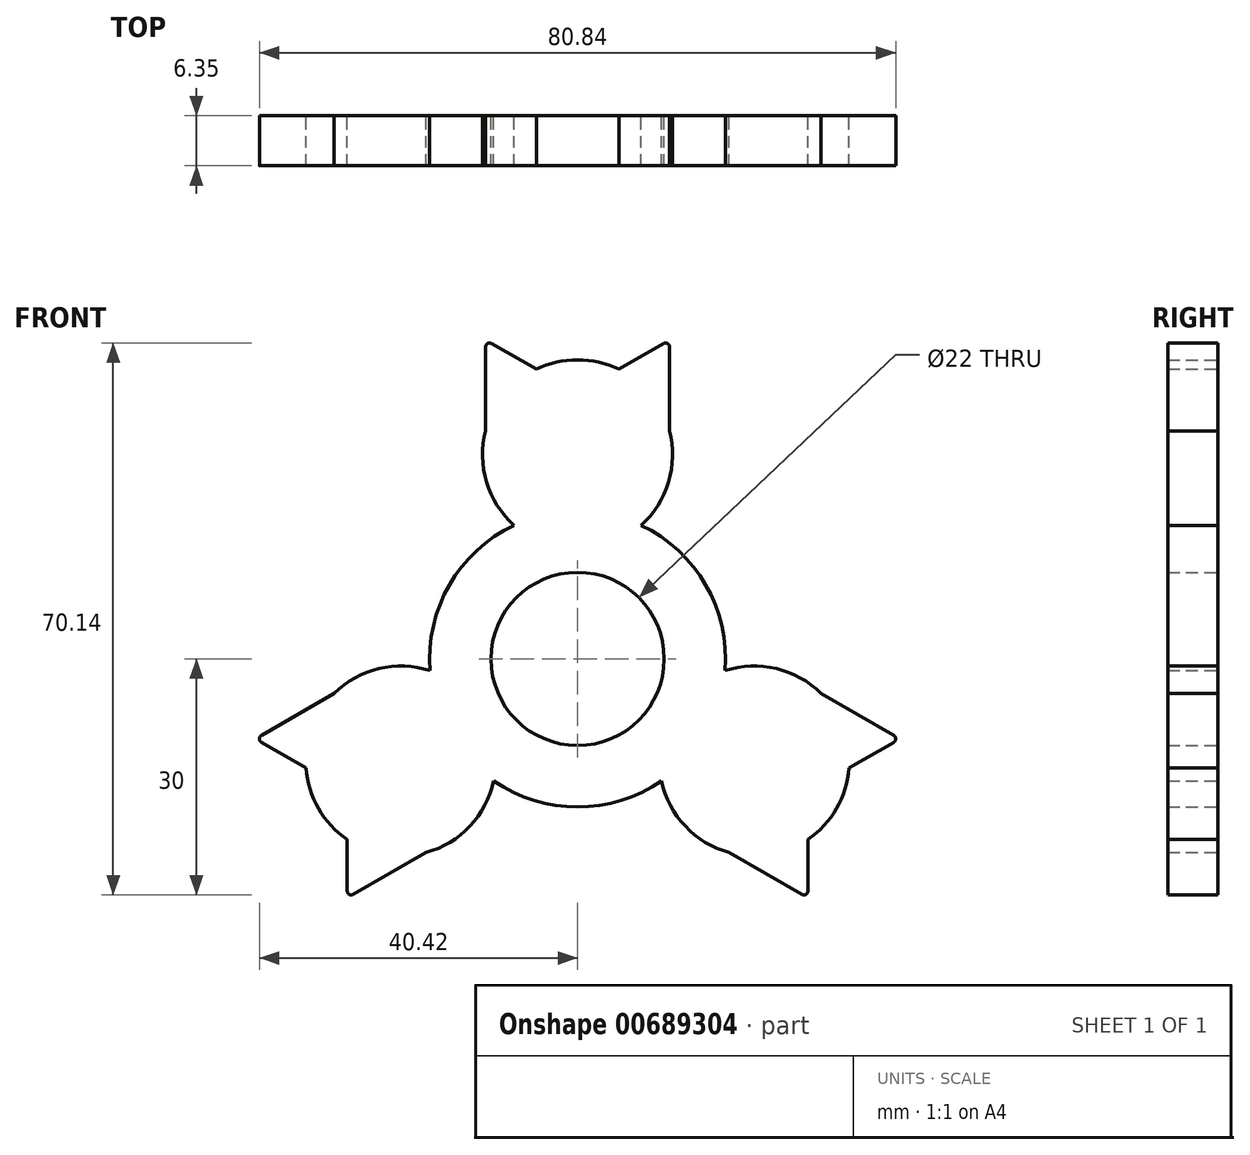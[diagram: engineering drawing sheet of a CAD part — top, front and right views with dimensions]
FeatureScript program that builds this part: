
annotation { "Feature Type Name" : "Feature", "Feature Type Description" : "" }
export const myFeature = defineFeature(function(context is Context, id is Id, definition is map)
    precondition{}
    {
        {
            var Q0;
            Q0=qCreatedBy(makeId("Front.planeOp"),FACE);
            var sketch = newSketch(context, id + "F0", { "sketchPlane" : qUnion([Q0])});
            skCircle(sketch, "E0", {"center": v(0, 0) * mm, "radius": 44.45 * mm, "construction": true});
            skCircle(sketch, "E1", {"center": v(0, 0) * mm, "radius": 11 * mm});
            skCircle(sketch, "E2", {"center": v(0, 0) * mm, "radius": 4 * mm});
            skArc(sketch, "E3", {"start": v(18.74, -1.5) * mm, "mid": v(16.28, 9.4) * mm, "end": v(8.08, 16.97) * mm});
            skArc(sketch, "E4", {"start": v(8.08, 16.97) * mm, "mid": v(0, 38) * mm, "end": v(-8.08, 16.97) * mm});
            skLineSegment(sketch, "E5", {"start": v(-11.67, 28.98) * mm, "end": v(-11.67, 40.52) * mm});
            skLineSegment(sketch, "E6", {"start": v(-11.67, 40.52) * mm, "end": v(-5.24, 36.8) * mm});
            skLineSegment(sketch, "E7.MirrorCS", {"start": v(11.67, 40.52) * mm, "end": v(5.24, 36.8) * mm});
            skLineSegment(sketch, "E8.MirrorCS", {"start": v(11.67, 28.98) * mm, "end": v(11.67, 40.52) * mm});
            skArc(sketch, "E9.1.0", {"start": v(-18.74, -1.5) * mm, "mid": v(-32.9, -19) * mm, "end": v(-10.66, -15.48) * mm});
            skLineSegment(sketch, "E9.1.1", {"start": v(-40.92, -10.15) * mm, "end": v(-34.5, -13.86) * mm});
            skLineSegment(sketch, "E9.1.2", {"start": v(-30.94, -4.38) * mm, "end": v(-40.92, -10.15) * mm});
            skLineSegment(sketch, "E9.1.3", {"start": v(-29.25, -30.37) * mm, "end": v(-29.25, -22.94) * mm});
            skLineSegment(sketch, "E9.1.4", {"start": v(-19.26, -24.6) * mm, "end": v(-29.25, -30.37) * mm});
            skArc(sketch, "E9.2.0", {"start": v(10.66, -15.48) * mm, "mid": v(32.9, -19) * mm, "end": v(18.74, -1.5) * mm});
            skLineSegment(sketch, "E9.2.1", {"start": v(29.25, -30.37) * mm, "end": v(29.25, -22.94) * mm});
            skLineSegment(sketch, "E9.2.2", {"start": v(19.26, -24.6) * mm, "end": v(29.25, -30.37) * mm});
            skLineSegment(sketch, "E9.2.3", {"start": v(40.92, -10.15) * mm, "end": v(34.5, -13.86) * mm});
            skLineSegment(sketch, "E9.2.4", {"start": v(30.94, -4.38) * mm, "end": v(40.92, -10.15) * mm});
            skLineSegment(sketch, "E10", {"start": v(0, 25.93) * mm, "end": v(0, 0) * mm, "construction": true});
            skLineSegment(sketch, "E11", {"start": v(0, 0) * mm, "end": v(22.46, -12.97) * mm, "construction": true});
            skLineSegment(sketch, "E12", {"start": v(0, 0) * mm, "end": v(-22.46, -12.97) * mm, "construction": true});
            skArc(sketch, "E13.trimOffspring", {"start": v(-10.66, -15.48) * mm, "mid": v(0, -18.8) * mm, "end": v(10.66, -15.48) * mm});
            skArc(sketch, "E14.trimOffspring", {"start": v(-8.08, 16.97) * mm, "mid": v(-16.28, 9.4) * mm, "end": v(-18.74, -1.5) * mm});
            skSolve(sketch);
        }
        {
            var Q0;
            Q0 = qSketchRegion(id + "F0", true);
            extrude(context, id + "F1", {"entities" : qUnion([Q0]), "depth" : 6.35 * mm, "offsetDistance" : 25.4 * mm});
        }
        {
            var Q0;
            Q0=makeQuery(id+"F1.opExtrude","SWEPT_EDGE",EDGE,{"disambiguationData":[OSD([sQuery(id+"F0.wireOp",EDGE,"E5"),sQuery(id+"F0.wireOp",EDGE,"E6")])]});
            var Q1;
            Q1=makeQuery(id+"F1.opExtrude","SWEPT_EDGE",EDGE,{"disambiguationData":[OSD([sQuery(id+"F0.wireOp",EDGE,"E7.MirrorCS"),sQuery(id+"F0.wireOp",EDGE,"E8.MirrorCS")])]});
            var Q2;
            Q2=makeQuery(id+"F1.opExtrude","SWEPT_EDGE",EDGE,{"disambiguationData":[OSD([sQuery(id+"F0.wireOp",EDGE,"E9.2.3"),sQuery(id+"F0.wireOp",EDGE,"E9.2.4")])]});
            var Q3;
            Q3=makeQuery(id+"F1.opExtrude","SWEPT_EDGE",EDGE,{"disambiguationData":[OSD([sQuery(id+"F0.wireOp",EDGE,"E9.2.1"),sQuery(id+"F0.wireOp",EDGE,"E9.2.2")])]});
            var Q4;
            Q4=makeQuery(id+"F1.opExtrude","SWEPT_EDGE",EDGE,{"disambiguationData":[OSD([sQuery(id+"F0.wireOp",EDGE,"E9.1.3"),sQuery(id+"F0.wireOp",EDGE,"E9.1.4")])]});
            var Q5;
            Q5=makeQuery(id+"F1.opExtrude","SWEPT_EDGE",EDGE,{"disambiguationData":[OSD([sQuery(id+"F0.wireOp",EDGE,"E9.1.1"),sQuery(id+"F0.wireOp",EDGE,"E9.1.2")])]});
            fillet(context, id + "F2", {"entities" : qUnion([Q0, Q1, Q2, Q3, Q4, Q5]), "radius" : 0.5 * mm, "tangentPropagation" : true, "allowEdgeOverflow" : false});
        }
    });
